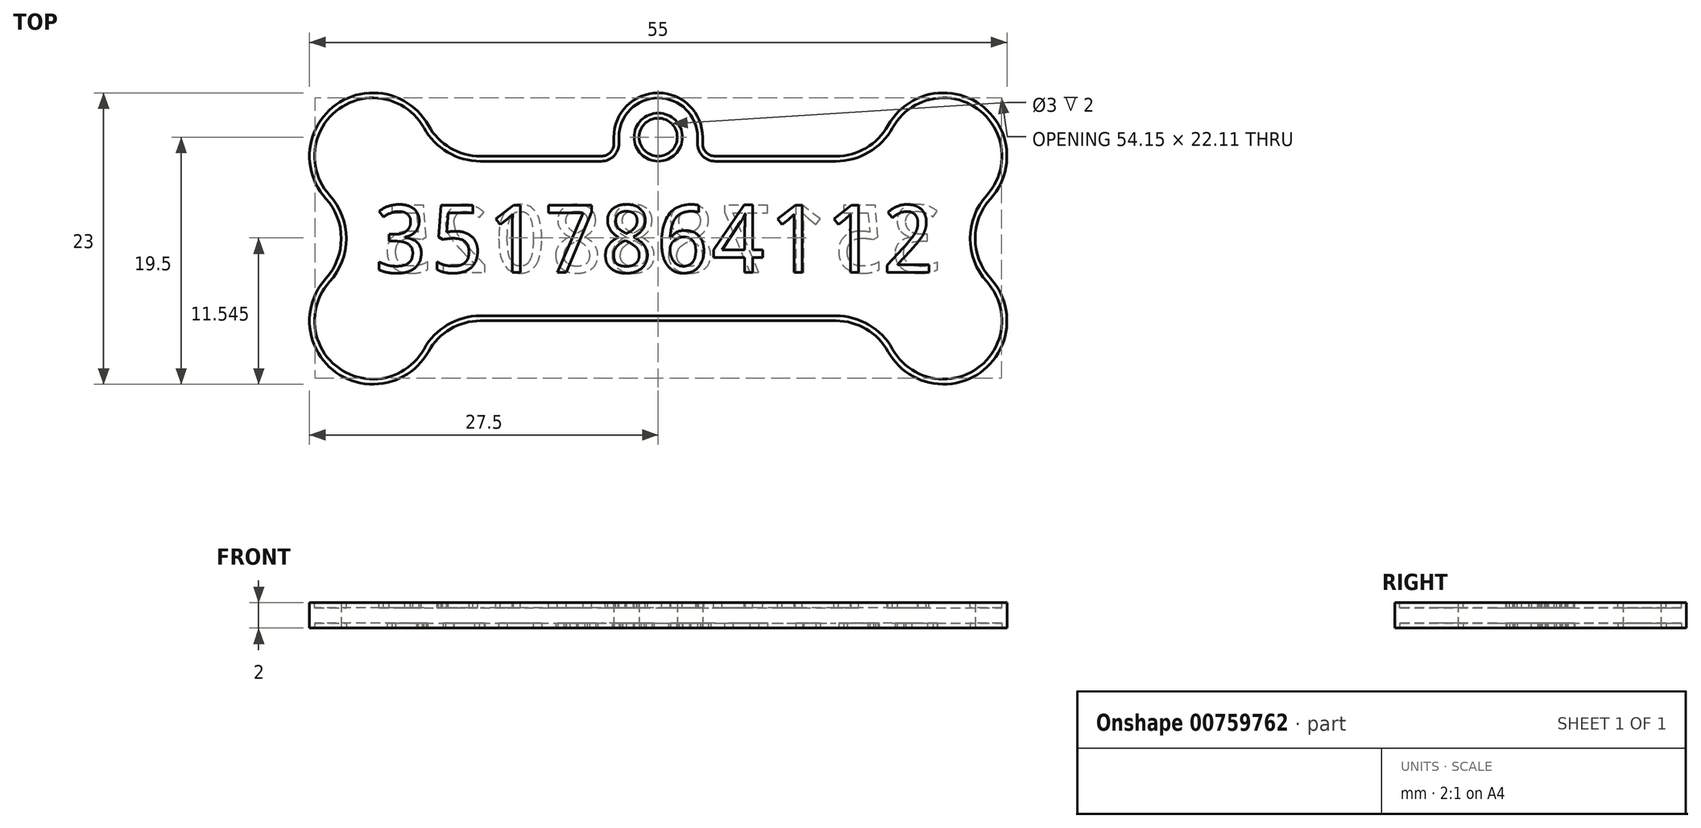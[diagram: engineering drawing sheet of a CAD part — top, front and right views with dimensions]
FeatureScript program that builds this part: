
annotation { "Feature Type Name" : "Feature", "Feature Type Description" : "" }
export const myFeature = defineFeature(function(context is Context, id is Id, definition is map)
    precondition{}
    {
        {
            var Q0;
            Q0=qCreatedBy(makeId("Top.planeOp"),FACE);
            var sketch = newSketch(context, id + "F0", { "sketchPlane" : qUnion([Q0])});
            skLineSegment(sketch, "E0.bottom", {"start": v(-14.01, -6.5) * mm, "end": v(14.01, -6.5) * mm});
            skLineSegment(sketch, "E0.top", {"start": v(-14.01, 6.5) * mm, "end": v(-4.5, 6.5) * mm});
            skArc(sketch, "E1", {"start": v(26.21, 3.15) * mm, "mid": v(25.4, 10.57) * mm, "end": v(18.13, 8.92) * mm});
            skArc(sketch, "E2", {"start": v(18.13, -8.92) * mm, "mid": v(25.4, -10.57) * mm, "end": v(26.21, -3.15) * mm});
            skArc(sketch, "E3", {"start": v(-18.13, 8.92) * mm, "mid": v(-25.4, 10.57) * mm, "end": v(-26.21, 3.15) * mm});
            skArc(sketch, "E4", {"start": v(-26.21, -3.15) * mm, "mid": v(-25.4, -10.57) * mm, "end": v(-18.13, -8.92) * mm});
            skArc(sketch, "E5", {"start": v(26.21, 3.15) * mm, "mid": v(25, 0) * mm, "end": v(26.21, -3.15) * mm});
            skArc(sketch, "E6", {"start": v(-26.21, -3.15) * mm, "mid": v(-25, 0) * mm, "end": v(-26.21, 3.15) * mm});
            skPoint(sketch, "E7.visualSharp", {"position": v(-17.5, 6.5) * mm});
            skArc(sketch, "E7.filletArc", {"start": v(-18.13, 8.92) * mm, "mid": v(-16.4, 7.15) * mm, "end": v(-14.01, 6.5) * mm});
            skPoint(sketch, "E8.visualSharp", {"position": v(17.5, 6.5) * mm});
            skArc(sketch, "E8.filletArc", {"start": v(14.01, 6.5) * mm, "mid": v(16.4, 7.15) * mm, "end": v(18.13, 8.92) * mm});
            skPoint(sketch, "E9.visualSharp", {"position": v(17.5, -6.5) * mm});
            skArc(sketch, "E9.filletArc", {"start": v(18.13, -8.92) * mm, "mid": v(16.4, -7.15) * mm, "end": v(14.01, -6.5) * mm});
            skPoint(sketch, "E10.visualSharp", {"position": v(-17.5, -6.5) * mm});
            skArc(sketch, "E10.filletArc", {"start": v(-14.01, -6.5) * mm, "mid": v(-16.4, -7.15) * mm, "end": v(-18.13, -8.92) * mm});
            skLineSegment(sketch, "E11", {"start": v(3.5, 8) * mm, "end": v(3.5, 7.5) * mm});
            skLineSegment(sketch, "E12", {"start": v(-3.5, 8) * mm, "end": v(-3.5, 7.5) * mm});
            skArc(sketch, "E13", {"start": v(3.5, 8) * mm, "mid": v(0, 11.5) * mm, "end": v(-3.5, 8) * mm});
            skLineSegment(sketch, "E14.trimOffspring", {"start": v(4.5, 6.5) * mm, "end": v(14.01, 6.5) * mm});
            skCircle(sketch, "E15", {"center": v(0, 8) * mm, "radius": 1.5 * mm});
            skPoint(sketch, "E16.visualSharp", {"position": v(-3.5, 6.5) * mm});
            skArc(sketch, "E16.filletArc", {"start": v(-4.5, 6.5) * mm, "mid": v(-3.8, 6.8) * mm, "end": v(-3.5, 7.5) * mm});
            skPoint(sketch, "E17.visualSharp", {"position": v(3.5, 6.5) * mm});
            skArc(sketch, "E17.filletArc", {"start": v(3.5, 7.5) * mm, "mid": v(3.8, 6.8) * mm, "end": v(4.5, 6.5) * mm});
            skSolve(sketch);
        }
        {
            var Q0;
            Q0=makeQuery(id+"F0.imprint","IMPRINT",FACE,{"disambiguationData":[TD([[makeQuery(id+"F0.imprint","IMPRINT",EDGE,{"derivedFrom":sQuery(id+"F0.wireOp",EDGE,"E0.bottom")}),1.0]])]});
            extrude(context, id + "F1", {"entities" : qUnion([Q0]), "depth" : 2 * mm, "offsetDistance" : 25 * mm});
        }
        {
            var Q0;
            Q0=makeQuery(id+"F1.opExtrude","CAP_FACE",FACE,{"disambiguationData":[OSD([sQuery(id+"F0.wireOp",EDGE,"E0.bottom"),sQuery(id+"F0.wireOp",EDGE,"E0.top"),sQuery(id+"F0.wireOp",EDGE,"E1"),sQuery(id+"F0.wireOp",EDGE,"E2"),sQuery(id+"F0.wireOp",EDGE,"E3"),sQuery(id+"F0.wireOp",EDGE,"E4"),sQuery(id+"F0.wireOp",EDGE,"E5"),sQuery(id+"F0.wireOp",EDGE,"E6"),sQuery(id+"F0.wireOp",EDGE,"E7.filletArc"),sQuery(id+"F0.wireOp",EDGE,"E8.filletArc"),sQuery(id+"F0.wireOp",EDGE,"E9.filletArc"),sQuery(id+"F0.wireOp",EDGE,"E10.filletArc"),sQuery(id+"F0.wireOp",EDGE,"E11"),sQuery(id+"F0.wireOp",EDGE,"E12"),sQuery(id+"F0.wireOp",EDGE,"E13"),sQuery(id+"F0.wireOp",EDGE,"E14.trimOffspring"),sQuery(id+"F0.wireOp",EDGE,"E15"),sQuery(id+"F0.wireOp",EDGE,"E16.filletArc"),sQuery(id+"F0.wireOp",EDGE,"E17.filletArc")])],"isStart":false});
            var sketch = newSketch(context, id + "F2", { "sketchPlane" : qUnion([Q0])});
            skText(sketch, "E18", { "text": "3517864112", "fontName": "DroidSansMono.ttf"});
            skLineSegment(sketch, "E19.0", {"start": v(3.1, 7.5) * mm, "end": v(3.1, 8) * mm});
            skArc(sketch, "E19.1", {"start": v(4.5, 6.1) * mm, "mid": v(3.51, 6.51) * mm, "end": v(3.1, 7.5) * mm});
            skLineSegment(sketch, "E19.2", {"start": v(14.01, 6.1) * mm, "end": v(4.5, 6.1) * mm});
            skArc(sketch, "E19.3", {"start": v(18.48, 8.73) * mm, "mid": v(16.6, 6.8) * mm, "end": v(14.01, 6.1) * mm});
            skArc(sketch, "E19.4", {"start": v(25.91, 3.42) * mm, "mid": v(25.17, 10.24) * mm, "end": v(18.48, 8.73) * mm});
            skArc(sketch, "E19.5", {"start": v(3.1, 8) * mm, "mid": v(0, 11.1) * mm, "end": v(-3.1, 8) * mm});
            skArc(sketch, "E19.6", {"start": v(25.91, -3.42) * mm, "mid": v(24.6, 0) * mm, "end": v(25.91, 3.42) * mm});
            skArc(sketch, "E19.7", {"start": v(18.48, -8.73) * mm, "mid": v(25.17, -10.24) * mm, "end": v(25.91, -3.42) * mm});
            skArc(sketch, "E19.8", {"start": v(-14.01, 6.1) * mm, "mid": v(-16.6, 6.8) * mm, "end": v(-18.48, 8.73) * mm});
            skLineSegment(sketch, "E19.9", {"start": v(-4.5, 6.1) * mm, "end": v(-14.01, 6.1) * mm});
            skArc(sketch, "E19.10", {"start": v(-3.1, 7.5) * mm, "mid": v(-3.51, 6.51) * mm, "end": v(-4.5, 6.1) * mm});
            skLineSegment(sketch, "E19.11", {"start": v(-3.1, 8) * mm, "end": v(-3.1, 7.5) * mm});
            skArc(sketch, "E19.12", {"start": v(-18.48, 8.73) * mm, "mid": v(-25.17, 10.24) * mm, "end": v(-25.91, 3.42) * mm});
            skArc(sketch, "E19.13", {"start": v(-25.91, 3.42) * mm, "mid": v(-24.6, 0) * mm, "end": v(-25.91, -3.42) * mm});
            skArc(sketch, "E19.14", {"start": v(-25.91, -3.42) * mm, "mid": v(-25.17, -10.24) * mm, "end": v(-18.48, -8.73) * mm});
            skArc(sketch, "E19.15", {"start": v(-18.48, -8.73) * mm, "mid": v(-16.6, -6.8) * mm, "end": v(-14.01, -6.1) * mm});
            skLineSegment(sketch, "E19.16", {"start": v(-14.01, -6.1) * mm, "end": v(14.01, -6.1) * mm});
            skArc(sketch, "E19.17", {"start": v(14.01, -6.1) * mm, "mid": v(16.6, -6.8) * mm, "end": v(18.48, -8.73) * mm});
            skCircle(sketch, "E20.0", {"center": v(0, 8) * mm, "radius": 1.9 * mm});
            const initialGuessF2  = {"E18": [-0.0225, -0.00267, 1, 0, 0.00533]};
            skSetInitialGuess(sketch, initialGuessF2);
            skSolve(sketch);
        }
        {
            var Q0;
            Q0 = qSketchRegion(id + "F2", true);
            var Q1;
            Q1=makeQuery(id+"F2.imprint","IMPRINT",FACE,{"disambiguationData":[TD([[makeQuery(id+"F2.imprint","IMPRINT",EDGE,{"derivedFrom":sQuery(id+"F2.wireOp",EDGE,"E18.sketch_text.stroke-75")}),1.0]])]});
            var Q2;
            Q2=makeQuery(id+"F2.imprint","IMPRINT",FACE,{"disambiguationData":[TD([[makeQuery(id+"F2.imprint","IMPRINT",EDGE,{"derivedFrom":sQuery(id+"F2.wireOp",EDGE,"E18.sketch_text.stroke-96")}),1.0]])]});
            var Q3;
            Q3=makeQuery(id+"F2.imprint","IMPRINT",FACE,{"disambiguationData":[TD([[makeQuery(id+"F2.imprint","IMPRINT",EDGE,{"derivedFrom":sQuery(id+"F2.wireOp",EDGE,"E18.sketch_text.stroke-115")}),1.0]])]});
            var Q4;
            Q4=makeQuery(id+"F2.imprint","IMPRINT",FACE,{"disambiguationData":[TD([[makeQuery(id+"F2.imprint","IMPRINT",EDGE,{"derivedFrom":sQuery(id+"F2.wireOp",EDGE,"E18.sketch_text.stroke-68")}),1.0]])]});
            extrude(context, id + "F3", {"entities" : qUnion([Q0, Q1, Q2, Q3, Q4]), "operationType" : NewBodyOperationType.REMOVE, "oppositeDirection" : true, "depth" : 0.4 * mm, "offsetDistance" : 25 * mm});
        }
        {
            var Q0;
            Q0=makeQuery(id+"F1.opExtrude","CAP_FACE",FACE,{"disambiguationData":[OSD([sQuery(id+"F0.wireOp",EDGE,"E0.bottom"),sQuery(id+"F0.wireOp",EDGE,"E0.top"),sQuery(id+"F0.wireOp",EDGE,"E1"),sQuery(id+"F0.wireOp",EDGE,"E2"),sQuery(id+"F0.wireOp",EDGE,"E3"),sQuery(id+"F0.wireOp",EDGE,"E4"),sQuery(id+"F0.wireOp",EDGE,"E5"),sQuery(id+"F0.wireOp",EDGE,"E6"),sQuery(id+"F0.wireOp",EDGE,"E7.filletArc"),sQuery(id+"F0.wireOp",EDGE,"E8.filletArc"),sQuery(id+"F0.wireOp",EDGE,"E9.filletArc"),sQuery(id+"F0.wireOp",EDGE,"E10.filletArc"),sQuery(id+"F0.wireOp",EDGE,"E11"),sQuery(id+"F0.wireOp",EDGE,"E12"),sQuery(id+"F0.wireOp",EDGE,"E13"),sQuery(id+"F0.wireOp",EDGE,"E14.trimOffspring"),sQuery(id+"F0.wireOp",EDGE,"E15"),sQuery(id+"F0.wireOp",EDGE,"E16.filletArc"),sQuery(id+"F0.wireOp",EDGE,"E17.filletArc")])],"isStart":true});
            var sketch = newSketch(context, id + "F4", { "sketchPlane" : qUnion([Q0])});
            skText(sketch, "E21", { "text": "3517888025", "fontName": "DroidSansMono.ttf"});
            skCircle(sketch, "E22.0", {"center": v(0, -8) * mm, "radius": 1.9 * mm});
            skLineSegment(sketch, "E23.0", {"start": v(3.1, -8) * mm, "end": v(3.1, -7.5) * mm});
            skArc(sketch, "E23.1", {"start": v(3.1, -7.5) * mm, "mid": v(3.51, -6.51) * mm, "end": v(4.5, -6.1) * mm});
            skLineSegment(sketch, "E23.2", {"start": v(4.5, -6.1) * mm, "end": v(14.01, -6.1) * mm});
            skArc(sketch, "E23.3", {"start": v(14.01, -6.1) * mm, "mid": v(16.6, -6.8) * mm, "end": v(18.48, -8.73) * mm});
            skArc(sketch, "E23.4", {"start": v(25.91, -3.42) * mm, "mid": v(25.17, -10.24) * mm, "end": v(18.48, -8.73) * mm});
            skArc(sketch, "E23.5", {"start": v(3.1, -8) * mm, "mid": v(0, -11.1) * mm, "end": v(-3.1, -8) * mm});
            skArc(sketch, "E23.6", {"start": v(25.91, -3.42) * mm, "mid": v(24.6, 0) * mm, "end": v(25.91, 3.42) * mm});
            skArc(sketch, "E23.7", {"start": v(18.48, 8.73) * mm, "mid": v(25.17, 10.24) * mm, "end": v(25.91, 3.42) * mm});
            skArc(sketch, "E23.8", {"start": v(-18.48, -8.73) * mm, "mid": v(-16.6, -6.8) * mm, "end": v(-14.01, -6.1) * mm});
            skLineSegment(sketch, "E23.9", {"start": v(-14.01, -6.1) * mm, "end": v(-4.5, -6.1) * mm});
            skArc(sketch, "E23.10", {"start": v(-4.5, -6.1) * mm, "mid": v(-3.51, -6.51) * mm, "end": v(-3.1, -7.5) * mm});
            skLineSegment(sketch, "E23.11", {"start": v(-3.1, -8) * mm, "end": v(-3.1, -7.5) * mm});
            skArc(sketch, "E23.12", {"start": v(-18.48, -8.73) * mm, "mid": v(-25.17, -10.24) * mm, "end": v(-25.91, -3.42) * mm});
            skArc(sketch, "E23.13", {"start": v(-25.91, 3.42) * mm, "mid": v(-24.6, 0) * mm, "end": v(-25.91, -3.42) * mm});
            skArc(sketch, "E23.14", {"start": v(-25.91, 3.42) * mm, "mid": v(-25.17, 10.24) * mm, "end": v(-18.48, 8.73) * mm});
            skArc(sketch, "E23.15", {"start": v(-14.01, 6.1) * mm, "mid": v(-16.6, 6.8) * mm, "end": v(-18.48, 8.73) * mm});
            skLineSegment(sketch, "E23.16", {"start": v(-14.01, 6.1) * mm, "end": v(14.01, 6.1) * mm});
            skArc(sketch, "E23.17", {"start": v(18.48, 8.73) * mm, "mid": v(16.6, 6.8) * mm, "end": v(14.01, 6.1) * mm});
            const initialGuessF4  = {"E21": [0.0225, 0.00267, -1, 0, 0.00534]};
            skSetInitialGuess(sketch, initialGuessF4);
            skSolve(sketch);
        }
        {
            var Q0;
            Q0 = qSketchRegion(id + "F4", true);
            var Q1;
            Q1=makeQuery(id+"F4.imprint","IMPRINT",FACE,{"disambiguationData":[TD([[makeQuery(id+"F4.imprint","IMPRINT",EDGE,{"derivedFrom":sQuery(id+"F4.wireOp",EDGE,"E21.sketch_text.stroke-68")}),1.0]])]});
            var Q2;
            Q2=makeQuery(id+"F4.imprint","IMPRINT",FACE,{"disambiguationData":[TD([[makeQuery(id+"F4.imprint","IMPRINT",EDGE,{"derivedFrom":sQuery(id+"F4.wireOp",EDGE,"E21.sketch_text.stroke-101")}),1.0]])]});
            var Q3;
            Q3=makeQuery(id+"F4.imprint","IMPRINT",FACE,{"disambiguationData":[TD([[makeQuery(id+"F4.imprint","IMPRINT",EDGE,{"derivedFrom":sQuery(id+"F4.wireOp",EDGE,"E21.sketch_text.stroke-75")}),1.0]])]});
            var Q4;
            Q4=makeQuery(id+"F4.imprint","IMPRINT",FACE,{"disambiguationData":[TD([[makeQuery(id+"F4.imprint","IMPRINT",EDGE,{"derivedFrom":sQuery(id+"F4.wireOp",EDGE,"E21.sketch_text.stroke-120")}),1.0]])]});
            var Q5;
            Q5=makeQuery(id+"F4.imprint","IMPRINT",FACE,{"disambiguationData":[TD([[makeQuery(id+"F4.imprint","IMPRINT",EDGE,{"derivedFrom":sQuery(id+"F4.wireOp",EDGE,"E21.sketch_text.stroke-140")}),1.0]])]});
            var Q6;
            Q6=makeQuery(id+"F4.imprint","IMPRINT",FACE,{"disambiguationData":[TD([[makeQuery(id+"F4.imprint","IMPRINT",EDGE,{"derivedFrom":sQuery(id+"F4.wireOp",EDGE,"E21.sketch_text.stroke-127")}),1.0]])]});
            var Q7;
            Q7=makeQuery(id+"F4.imprint","IMPRINT",FACE,{"disambiguationData":[TD([[makeQuery(id+"F4.imprint","IMPRINT",EDGE,{"derivedFrom":sQuery(id+"F4.wireOp",EDGE,"E21.sketch_text.stroke-94")}),1.0]])]});
            extrude(context, id + "F5", {"entities" : qUnion([Q0, Q1, Q2, Q3, Q4, Q5, Q6, Q7]), "operationType" : NewBodyOperationType.REMOVE, "oppositeDirection" : true, "depth" : 0.4 * mm, "offsetDistance" : 25 * mm});
        }
    });
